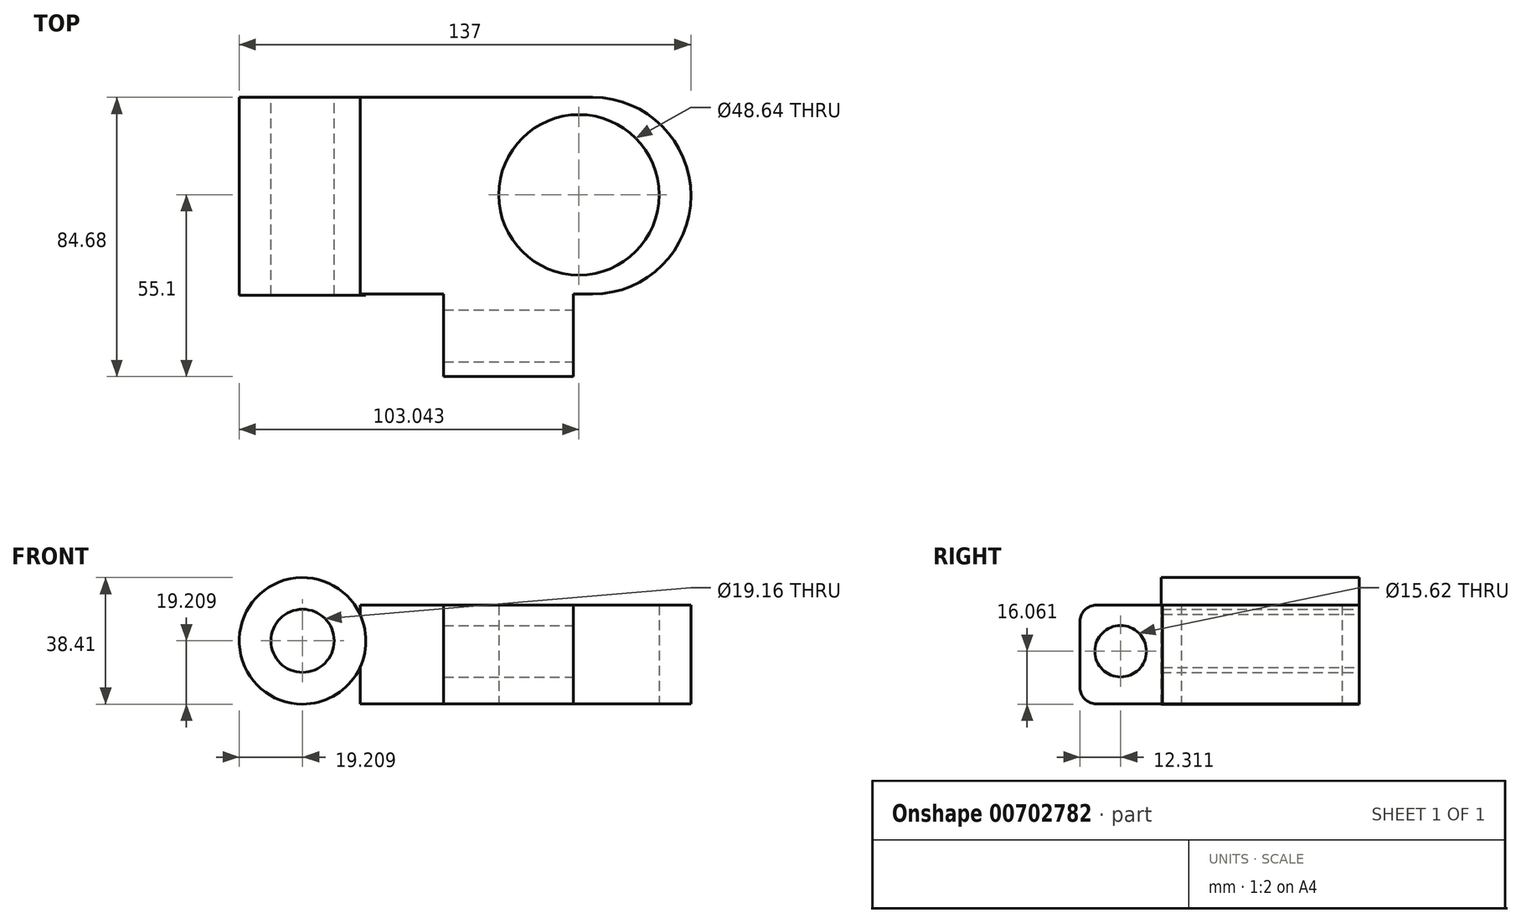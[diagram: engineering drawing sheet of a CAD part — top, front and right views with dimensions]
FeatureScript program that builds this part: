
annotation { "Feature Type Name" : "Feature", "Feature Type Description" : "" }
export const myFeature = defineFeature(function(context is Context, id is Id, definition is map)
    precondition{}
    {
        {
            var Q0;
            Q0=qCreatedBy(makeId("Front.planeOp"),FACE);
            var sketch = newSketch(context, id + "F0", { "sketchPlane" : qUnion([Q0])});
            skCircle(sketch, "E0", {"center": v(-77.85, 19.14) * mm, "radius": 19.2 * mm});
            skCircle(sketch, "E1", {"center": v(-77.85, 19.14) * mm, "radius": 9.58 * mm});
            skSolve(sketch);
        }
        {
            var Q0;
            Q0 = qSketchRegion(id + "F0", true);
            extrude(context, id + "F1", {"entities" : qUnion([Q0]), "depth" : 60 * mm, "offsetDistance" : 25 * mm});
        }
        {
            var Q0;
            Q0=qCreatedBy(makeId("Top.planeOp"),FACE);
            var sketch = newSketch(context, id + "F2", { "sketchPlane" : qUnion([Q0])});
            skLineSegment(sketch, "E2", {"start": v(-60.42, 0) * mm, "end": v(10.09, 0) * mm});
            skLineSegment(sketch, "E3", {"start": v(-60.42, -59.7) * mm, "end": v(10.09, -59.7) * mm});
            skArc(sketch, "E4", {"start": v(10.09, -59.7) * mm, "mid": v(39.94, -29.85) * mm, "end": v(10.09, 0) * mm});
            skLineSegment(sketch, "E5", {"start": v(-60.42, 0) * mm, "end": v(-60.42, -59.7) * mm});
            skCircle(sketch, "E6", {"center": v(5.98, -29.58) * mm, "radius": 24.32 * mm});
            skLineSegment(sketch, "E7", {"start": v(-35.09, -59.7) * mm, "end": v(-35.09, -84.68) * mm});
            skLineSegment(sketch, "E8", {"start": v(-35.09, -84.68) * mm, "end": v(4.27, -84.68) * mm});
            skLineSegment(sketch, "E9", {"start": v(4.27, -84.68) * mm, "end": v(4.27, -59.7) * mm});
            skSolve(sketch);
        }
        {
            var Q0;
            Q0 = qSketchRegion(id + "F2", true);
            extrude(context, id + "F3", {"entities" : qUnion([Q0]), "operationType" : NewBodyOperationType.ADD, "depth" : 30 * mm, "offsetDistance" : 25 * mm});
        }
        {
            var Q0;
            Q0=makeQuery(id+"F3.opExtrude","CAP_EDGE",EDGE,{"disambiguationData":[OSD([sQuery(id+"F2.wireOp",EDGE,"E8")])],"isStart":false});
            var Q1;
            Q1=makeQuery(id+"F3.opExtrude","CAP_EDGE",EDGE,{"disambiguationData":[OSD([sQuery(id+"F2.wireOp",EDGE,"E8")])],"isStart":true});
            fillet(context, id + "F4", {"entities" : qUnion([Q0, Q1]), "radius" : 5 * mm, "tangentPropagation" : true, "allowEdgeOverflow" : false});
        }
        {
            var Q0;
            Q0=makeQuery(id+"F3.opExtrude","SWEPT_FACE",FACE,{"disambiguationData":[OSD([sQuery(id+"F2.wireOp",EDGE,"E9")])]});
            var sketch = newSketch(context, id + "F5", { "sketchPlane" : qUnion([Q0])});
            skCircle(sketch, "E10", {"center": v(-72.37, 16) * mm, "radius": 7.81 * mm});
            skSolve(sketch);
        }
        {
            var Q0;
            Q0 = qSketchRegion(id + "F5", true);
            extrude(context, id + "F6", {"entities" : qUnion([Q0]), "operationType" : NewBodyOperationType.REMOVE, "oppositeDirection" : true, "depth" : 45 * mm, "offsetDistance" : 25 * mm});
        }
    });
